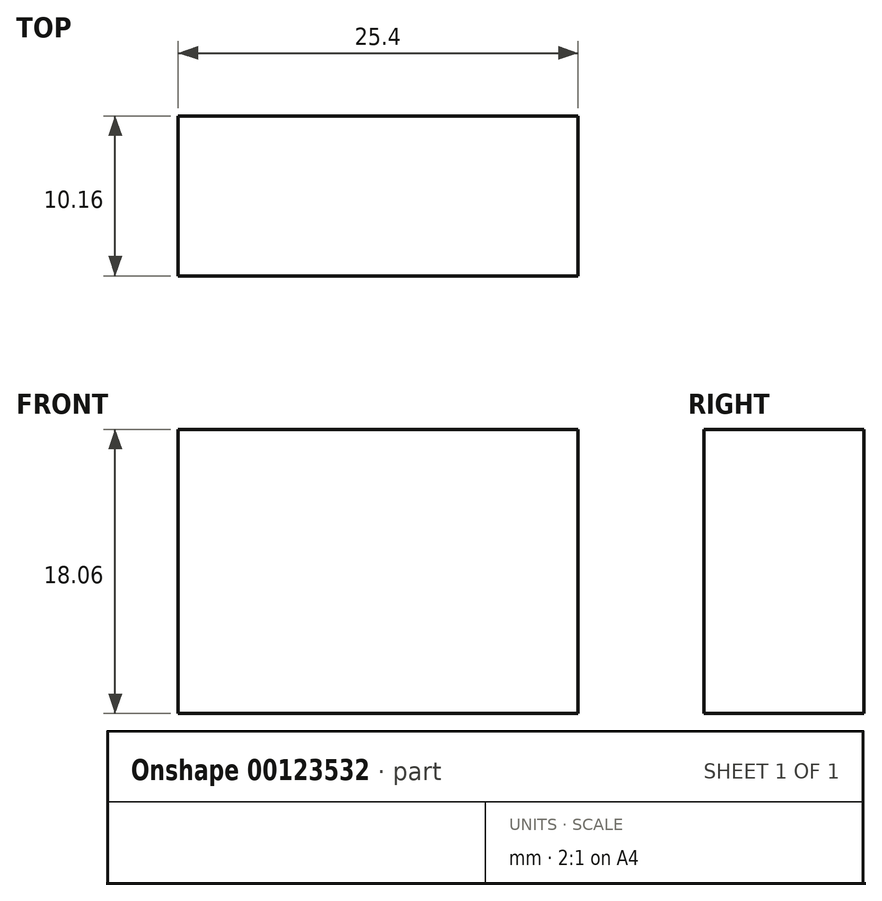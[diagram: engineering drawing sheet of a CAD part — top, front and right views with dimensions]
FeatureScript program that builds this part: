
annotation { "Feature Type Name" : "Feature", "Feature Type Description" : "" }
export const myFeature = defineFeature(function(context is Context, id is Id, definition is map)
    precondition{}
    {
        {
            var Q0;
            Q0=qCreatedBy(makeId("Front.planeOp"),FACE);
            var sketch = newSketch(context, id + "F0", { "sketchPlane" : qUnion([Q0])});
            skLineSegment(sketch, "E0.bottom", {"start": v(-25.4, 11.28) * mm, "end": v(0, 11.28) * mm});
            skLineSegment(sketch, "E0.top", {"start": v(-25.4, -6.78) * mm, "end": v(0, -6.78) * mm});
            skLineSegment(sketch, "E0.left", {"start": v(-25.4, 11.28) * mm, "end": v(-25.4, -6.78) * mm});
            skLineSegment(sketch, "E0.right", {"start": v(0, 11.28) * mm, "end": v(0, -6.78) * mm});
            skSolve(sketch);
        }
        {
            var Q0;
            Q0 = qSketchRegion(id + "F0", true);
            extrude(context, id + "F1", {"entities" : qUnion([Q0]), "depth" : 10.16 * mm});
        }
    });
